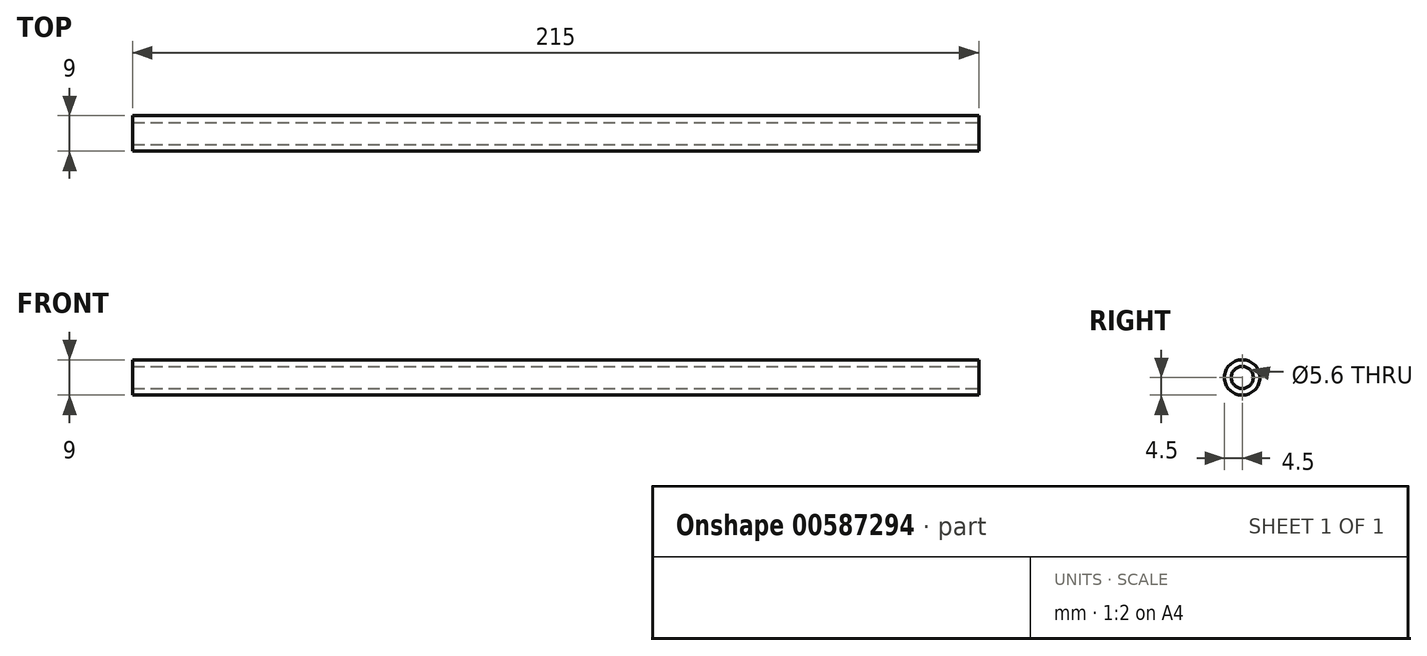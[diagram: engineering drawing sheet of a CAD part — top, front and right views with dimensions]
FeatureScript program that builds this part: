
annotation { "Feature Type Name" : "Feature", "Feature Type Description" : "" }
export const myFeature = defineFeature(function(context is Context, id is Id, definition is map)
    precondition{}
    {
        {
            var Q0;
            Q0=qCreatedBy(makeId("Right.planeOp"),FACE);
            var sketch = newSketch(context, id + "F0", { "sketchPlane" : qUnion([Q0])});
            skCircle(sketch, "E0", {"center": v(0, 0) * mm, "radius": 4.5 * mm});
            skSolve(sketch);
        }
        {
            var Q0;
            Q0=makeQuery(id+"F0.imprint","IMPRINT",FACE,{"disambiguationData":[TD([[makeQuery(id+"F0.imprint","IMPRINT",EDGE,{"derivedFrom":sQuery(id+"F0.wireOp",EDGE,"E0")}),1.0]])]});
            var Q1;
            Q1 = qConstructionFilter(qBodyType(qCreatedBy(id + "F0" ,EDGE), BodyType.WIRE), ConstructionObject.NO);
            extrude(context, id + "F1", {"entities" : qUnion([Q0]), "surfaceEntities" : qUnion([Q1]), "depth" : 215 * mm, "offsetDistance" : 25 * mm});
        }
        {
            var Q0;
            Q0=makeQuery(id+"F1.opExtrude","CAP_FACE",FACE,{"disambiguationData":[OSD([sQuery(id+"F0.wireOp",EDGE,"E0")])],"isStart":false});
            var sketch = newSketch(context, id + "F2", { "sketchPlane" : qUnion([Q0])});
            skCircle(sketch, "E1", {"center": v(0, 0) * mm, "radius": 2.8 * mm});
            skSolve(sketch);
        }
        {
            var Q0;
            Q0=makeQuery(id+"F2.imprint","IMPRINT",FACE,{"disambiguationData":[TD([[makeQuery(id+"F2.imprint","IMPRINT",EDGE,{"derivedFrom":sQuery(id+"F2.wireOp",EDGE,"E1")}),1.0]])]});
            extrude(context, id + "F3", {"entities" : qUnion([Q0]), "operationType" : NewBodyOperationType.REMOVE, "endBound" : BoundingType.UP_TO_NEXT, "oppositeDirection" : true, "depth" : 25 * mm, "offsetDistance" : 25 * mm});
        }
    });
